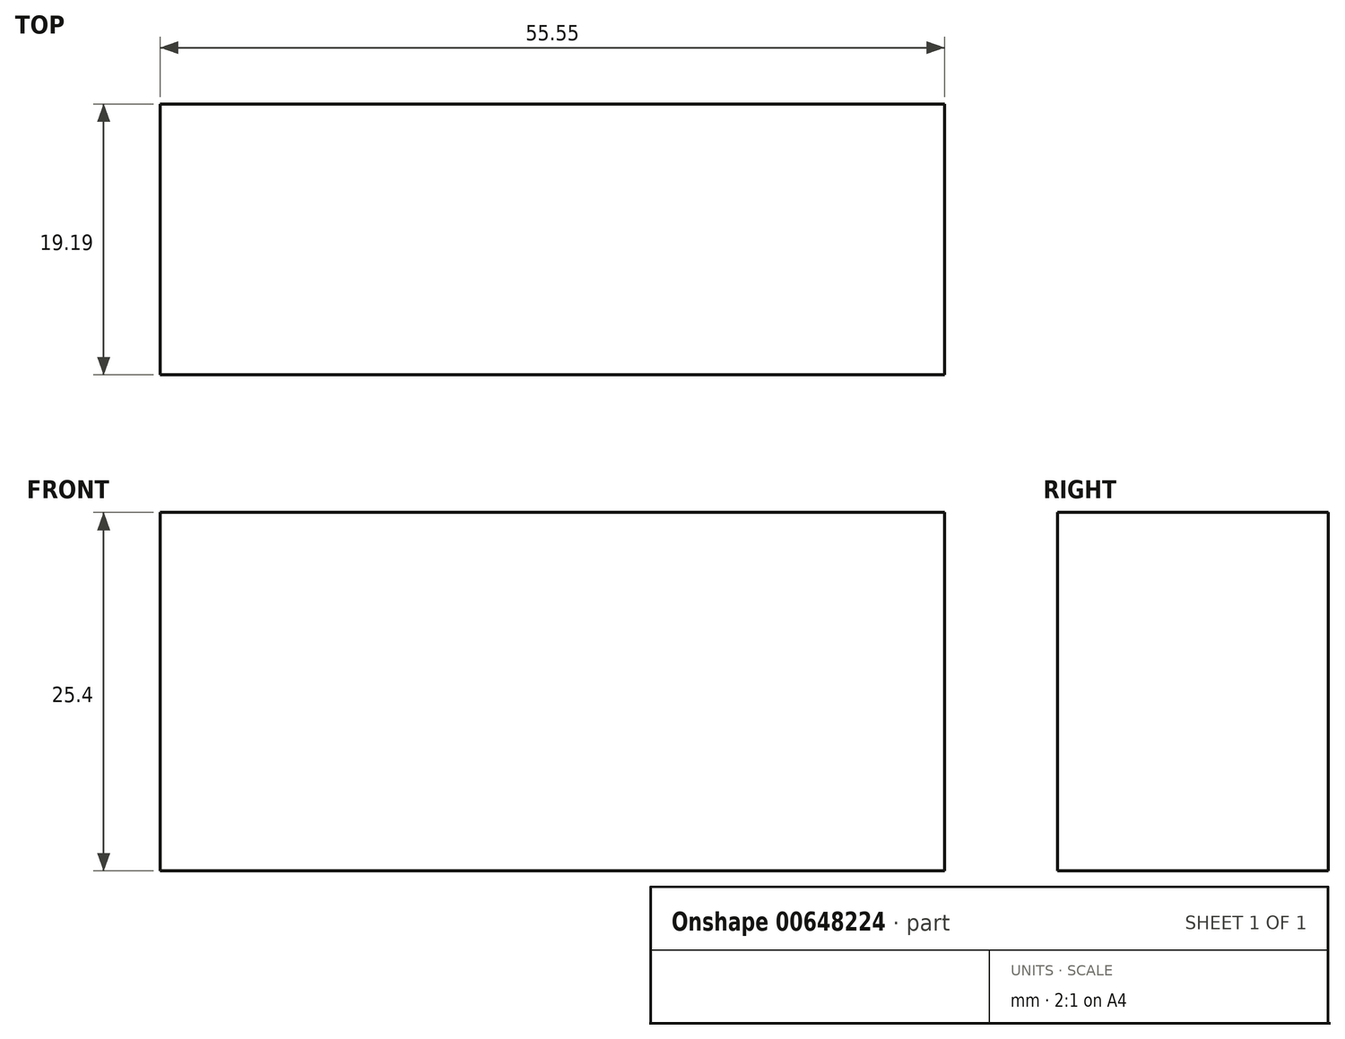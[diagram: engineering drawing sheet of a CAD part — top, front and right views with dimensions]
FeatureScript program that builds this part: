
annotation { "Feature Type Name" : "Feature", "Feature Type Description" : "" }
export const myFeature = defineFeature(function(context is Context, id is Id, definition is map)
    precondition{}
    {
        {
            var Q0;
            Q0=qCreatedBy(makeId("Top.planeOp"),FACE);
            var sketch = newSketch(context, id + "F0", { "sketchPlane" : qUnion([Q0])});
            skLineSegment(sketch, "E0.bottom", {"start": v(-136.1, 19.2) * mm, "end": v(-80.54, 19.2) * mm});
            skLineSegment(sketch, "E0.top", {"start": v(-136.1, 0) * mm, "end": v(-80.54, 0) * mm});
            skLineSegment(sketch, "E0.left", {"start": v(-136.1, 19.2) * mm, "end": v(-136.1, 0) * mm});
            skLineSegment(sketch, "E0.right", {"start": v(-80.54, 19.2) * mm, "end": v(-80.54, 0) * mm});
            skSolve(sketch);
        }
        {
            var Q0;
            Q0 = qSketchRegion(id + "F0", true);
            extrude(context, id + "F1", {"entities" : qUnion([Q0]), "depth" : 25.4 * mm, "offsetDistance" : 25.4 * mm});
        }
    });
